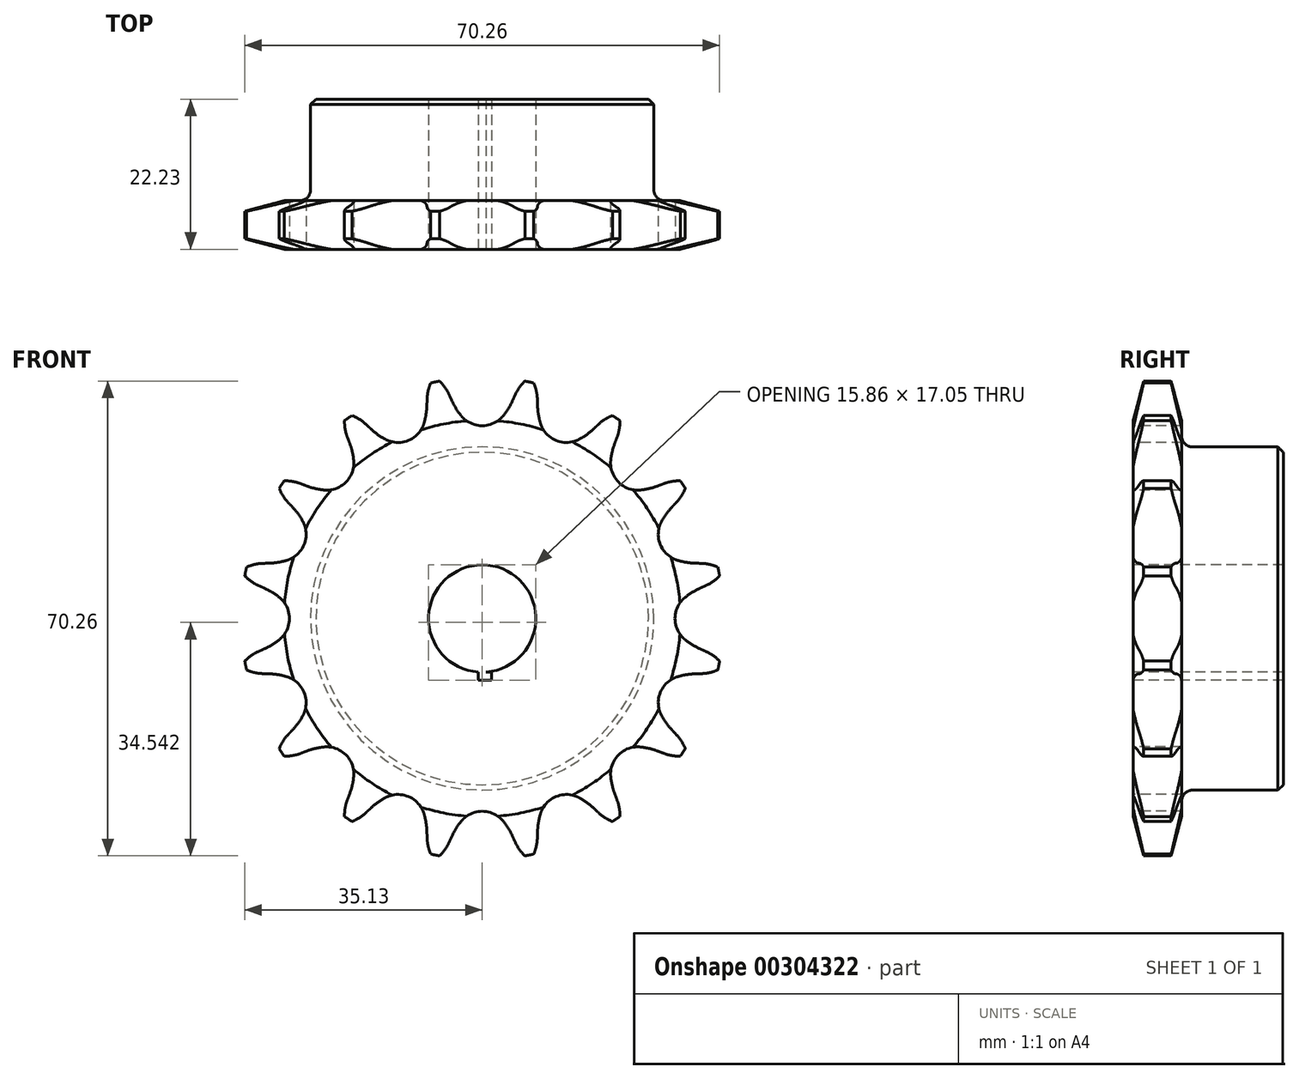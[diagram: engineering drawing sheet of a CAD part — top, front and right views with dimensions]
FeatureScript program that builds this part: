
annotation { "Feature Type Name" : "Feature", "Feature Type Description" : "" }
export const myFeature = defineFeature(function(context is Context, id is Id, definition is map)
    precondition{}
    {
        {
            var Q0;
            Q0=qCreatedBy(makeId("Right.planeOp"),FACE);
            var sketch = newSketch(context, id + "F0", { "sketchPlane" : qUnion([Q0])});
            skLineSegment(sketch, "E0", {"start": v(0, 0) * mm, "end": v(22.22, 0) * mm, "construction": true});
            skLineSegment(sketch, "E1", {"start": v(0, 35.69) * mm, "end": v(7.21, 35.69) * mm});
            skLineSegment(sketch, "E2", {"start": v(7.21, 35.69) * mm, "end": v(7.21, 25.4) * mm});
            skLineSegment(sketch, "E3", {"start": v(7.21, 25.4) * mm, "end": v(22.23, 25.4) * mm});
            skLineSegment(sketch, "E4", {"start": v(22.22, 25.4) * mm, "end": v(22.22, 7.94) * mm});
            skLineSegment(sketch, "E5", {"start": v(22.23, 7.94) * mm, "end": v(0, 7.94) * mm});
            skLineSegment(sketch, "E6", {"start": v(0, 7.94) * mm, "end": v(0, 35.69) * mm});
            skLineSegment(sketch, "E7.0.MirrorCS", {"start": v(0, -35.69) * mm, "end": v(7.21, -35.69) * mm});
            skLineSegment(sketch, "E7.1.MirrorCS", {"start": v(7.21, -35.69) * mm, "end": v(7.21, -25.4) * mm});
            skLineSegment(sketch, "E7.2.MirrorCS", {"start": v(22.23, -7.94) * mm, "end": v(0, -7.94) * mm});
            skLineSegment(sketch, "E7.3.MirrorCS", {"start": v(22.23, -25.4) * mm, "end": v(22.23, -7.94) * mm});
            skLineSegment(sketch, "E7.4.MirrorCS", {"start": v(7.21, -25.4) * mm, "end": v(22.23, -25.4) * mm});
            skLineSegment(sketch, "E7.5.MirrorCS", {"start": v(0, -7.94) * mm, "end": v(0, -35.69) * mm});
            skSolve(sketch);
        }
        {
            var Q0;
            Q0=makeQuery(id+"F0.imprint","IMPRINT",FACE,{"disambiguationData":[TD([[makeQuery(id+"F0.imprint","IMPRINT",EDGE,{"derivedFrom":sQuery(id+"F0.wireOp",EDGE,"E1")}),-1.0]])]});
            var Q1;
            Q1=sQuery(id+"F0.wireOp",EDGE,"E0");
            revolve(context, id + "F1", {"entities" : qUnion([Q0]), "axis" : qUnion([Q1]), "revolveType" : RevolveType.FULL});
        }
        {
            var Q0;
            Q0=makeQuery(id+"F1.opRevolve","SWEPT_EDGE",EDGE,{"disambiguationData":[OSD([sQuery(id+"F0.wireOp",EDGE,"E1"),sQuery(id+"F0.wireOp",EDGE,"E6")])]});
            var Q1;
            Q1=makeQuery(id+"F1.opRevolve","SWEPT_EDGE",EDGE,{"disambiguationData":[OSD([sQuery(id+"F0.wireOp",EDGE,"E1"),sQuery(id+"F0.wireOp",EDGE,"E2")])]});
            chamfer(context, id + "F2", {"entities" : qUnion([Q0, Q1]), "chamferType" : ChamferType.TWO_OFFSETS, "width1" : 6.35 * mm, "oppositeDirection" : false, "width2" : 1.57 * mm, "tangentPropagation" : true});
        }
        {
            var Q0;
            Q0=makeQuery(id+"F1.opRevolve","SWEPT_FACE",FACE,{"disambiguationData":[OSD([sQuery(id+"F0.wireOp",EDGE,"E6")])]});
            var sketch = newSketch(context, id + "F3", { "sketchPlane" : qUnion([Q0])});
            skCircle(sketch, "E8", {"center": v(0, 0) * mm, "radius": 32.55 * mm, "construction": true});
            skLineSegment(sketch, "E9", {"start": v(0, 0) * mm, "end": v(0, 32.55) * mm, "construction": true});
            skLineSegment(sketch, "E10", {"start": v(0, 32.55) * mm, "end": v(25.8, 32.55) * mm, "construction": true});
            skPoint(sketch, "E11", {"position": v(-10.88, 30.38) * mm});
            skPoint(sketch, "E12", {"position": v(4.95, 36.52) * mm});
            skLineSegment(sketch, "E13", {"start": v(0, 32.55) * mm, "end": v(4.95, 36.52) * mm, "construction": true});
            skLineSegment(sketch, "E14", {"start": v(4.95, 36.52) * mm, "end": v(-4.5, 32.26) * mm, "construction": true});
            skLineSegment(sketch, "E15", {"start": v(-4.5, 32.26) * mm, "end": v(-4.88, 33.1) * mm});
            skLineSegment(sketch, "E16", {"start": v(0, 0) * mm, "end": v(-7.12, 35.8) * mm, "construction": true});
            skArc(sketch, "E17", {"start": v(-7.12, 35.8) * mm, "mid": v(-15.95, 26.17) * mm, "end": v(-4.88, 33.1) * mm, "construction": true});
            skArc(sketch, "E18", {"start": v(-4.88, 33.1) * mm, "mid": v(-5.81, 34.6) * mm, "end": v(-7.12, 35.8) * mm});
            skArc(sketch, "E19", {"start": v(-3.14, 30.03) * mm, "mid": v(13.78, 41.93) * mm, "end": v(-4.5, 32.26) * mm, "construction": true});
            skArc(sketch, "E20", {"start": v(-4.5, 32.26) * mm, "mid": v(-3.89, 31.1) * mm, "end": v(-3.14, 30.03) * mm});
            skLineSegment(sketch, "E21", {"start": v(4.4, 12.5) * mm, "end": v(-4.88, 33.1) * mm, "construction": true});
            skArc(sketch, "E22.0.MirrorCS", {"start": v(4.5, 32.26) * mm, "mid": v(3.89, 31.1) * mm, "end": v(3.14, 30.03) * mm});
            skLineSegment(sketch, "E23.0.MirrorCS", {"start": v(4.5, 32.26) * mm, "end": v(4.88, 33.1) * mm});
            skArc(sketch, "E24.0.MirrorCS", {"start": v(4.88, 33.1) * mm, "mid": v(5.81, 34.6) * mm, "end": v(7.12, 35.8) * mm});
            skArc(sketch, "E25", {"start": v(-3.14, 30.03) * mm, "mid": v(0, 28.53) * mm, "end": v(3.14, 30.03) * mm});
            skArc(sketch, "E26", {"start": v(3.14, 30.03) * mm, "mid": v(0, 36.57) * mm, "end": v(-3.14, 30.03) * mm, "construction": true});
            skArc(sketch, "E27.1.0", {"start": v(-17.17, 28.7) * mm, "mid": v(-18.61, 29.74) * mm, "end": v(-20.28, 30.34) * mm});
            skLineSegment(sketch, "E27.1.1", {"start": v(-16.5, 28.08) * mm, "end": v(-17.17, 28.7) * mm});
            skArc(sketch, "E27.1.2", {"start": v(-16.5, 28.08) * mm, "mid": v(-15.5, 27.25) * mm, "end": v(-14.39, 26.55) * mm});
            skArc(sketch, "E27.1.3", {"start": v(-14.39, 26.55) * mm, "mid": v(-10.92, 26.36) * mm, "end": v(-8.6, 28.95) * mm});
            skArc(sketch, "E27.1.4", {"start": v(-8.19, 31.53) * mm, "mid": v(-8.3, 30.22) * mm, "end": v(-8.6, 28.95) * mm});
            skLineSegment(sketch, "E27.1.5", {"start": v(-8.19, 31.53) * mm, "end": v(-8.16, 32.44) * mm});
            skArc(sketch, "E27.1.6", {"start": v(-8.16, 32.44) * mm, "mid": v(-7.87, 34.19) * mm, "end": v(-7.12, 35.8) * mm});
            skArc(sketch, "E27.2.0", {"start": v(-26.85, 19.95) * mm, "mid": v(-28.57, 20.35) * mm, "end": v(-30.34, 20.28) * mm});
            skLineSegment(sketch, "E27.2.1", {"start": v(-26, 19.63) * mm, "end": v(-26.85, 19.95) * mm});
            skArc(sketch, "E27.2.2", {"start": v(-26, 19.63) * mm, "mid": v(-24.74, 19.24) * mm, "end": v(-23.45, 19.02) * mm});
            skArc(sketch, "E27.2.3", {"start": v(-23.45, 19.02) * mm, "mid": v(-20.17, 20.17) * mm, "end": v(-19.02, 23.45) * mm});
            skArc(sketch, "E27.2.4", {"start": v(-19.63, 26) * mm, "mid": v(-19.24, 24.74) * mm, "end": v(-19.02, 23.45) * mm});
            skLineSegment(sketch, "E27.2.5", {"start": v(-19.63, 26) * mm, "end": v(-19.95, 26.85) * mm});
            skArc(sketch, "E27.2.6", {"start": v(-19.95, 26.85) * mm, "mid": v(-20.35, 28.57) * mm, "end": v(-20.28, 30.34) * mm});
            skArc(sketch, "E27.3.0", {"start": v(-32.44, 8.16) * mm, "mid": v(-34.19, 7.87) * mm, "end": v(-35.8, 7.12) * mm});
            skLineSegment(sketch, "E27.3.1", {"start": v(-31.53, 8.19) * mm, "end": v(-32.44, 8.16) * mm});
            skArc(sketch, "E27.3.2", {"start": v(-31.53, 8.19) * mm, "mid": v(-30.22, 8.3) * mm, "end": v(-28.95, 8.6) * mm});
            skArc(sketch, "E27.3.3", {"start": v(-28.95, 8.6) * mm, "mid": v(-26.36, 10.92) * mm, "end": v(-26.55, 14.39) * mm});
            skArc(sketch, "E27.3.4", {"start": v(-28.08, 16.5) * mm, "mid": v(-27.25, 15.5) * mm, "end": v(-26.55, 14.39) * mm});
            skLineSegment(sketch, "E27.3.5", {"start": v(-28.08, 16.5) * mm, "end": v(-28.7, 17.17) * mm});
            skArc(sketch, "E27.3.6", {"start": v(-28.7, 17.17) * mm, "mid": v(-29.74, 18.61) * mm, "end": v(-30.34, 20.28) * mm});
            skArc(sketch, "E27.4.0", {"start": v(-33.1, -4.88) * mm, "mid": v(-34.6, -5.81) * mm, "end": v(-35.8, -7.12) * mm});
            skLineSegment(sketch, "E27.4.1", {"start": v(-32.26, -4.5) * mm, "end": v(-33.1, -4.88) * mm});
            skArc(sketch, "E27.4.2", {"start": v(-32.26, -4.5) * mm, "mid": v(-31.1, -3.89) * mm, "end": v(-30.03, -3.14) * mm});
            skArc(sketch, "E27.4.3", {"start": v(-30.03, -3.14) * mm, "mid": v(-28.53, 0) * mm, "end": v(-30.03, 3.14) * mm});
            skArc(sketch, "E27.4.4", {"start": v(-32.26, 4.5) * mm, "mid": v(-31.1, 3.89) * mm, "end": v(-30.03, 3.14) * mm});
            skLineSegment(sketch, "E27.4.5", {"start": v(-32.26, 4.5) * mm, "end": v(-33.1, 4.88) * mm});
            skArc(sketch, "E27.4.6", {"start": v(-33.1, 4.88) * mm, "mid": v(-34.6, 5.81) * mm, "end": v(-35.8, 7.12) * mm});
            skArc(sketch, "E27.5.0", {"start": v(-28.7, -17.17) * mm, "mid": v(-29.74, -18.61) * mm, "end": v(-30.34, -20.28) * mm});
            skLineSegment(sketch, "E27.5.1", {"start": v(-28.08, -16.5) * mm, "end": v(-28.7, -17.17) * mm});
            skArc(sketch, "E27.5.2", {"start": v(-28.08, -16.5) * mm, "mid": v(-27.25, -15.5) * mm, "end": v(-26.55, -14.39) * mm});
            skArc(sketch, "E27.5.3", {"start": v(-26.55, -14.39) * mm, "mid": v(-26.36, -10.92) * mm, "end": v(-28.95, -8.6) * mm});
            skArc(sketch, "E27.5.4", {"start": v(-31.53, -8.19) * mm, "mid": v(-30.22, -8.3) * mm, "end": v(-28.95, -8.6) * mm});
            skLineSegment(sketch, "E27.5.5", {"start": v(-31.53, -8.19) * mm, "end": v(-32.44, -8.16) * mm});
            skArc(sketch, "E27.5.6", {"start": v(-32.44, -8.16) * mm, "mid": v(-34.19, -7.87) * mm, "end": v(-35.8, -7.12) * mm});
            skArc(sketch, "E27.6.0", {"start": v(-19.95, -26.85) * mm, "mid": v(-20.35, -28.57) * mm, "end": v(-20.28, -30.34) * mm});
            skLineSegment(sketch, "E27.6.1", {"start": v(-19.63, -26) * mm, "end": v(-19.95, -26.85) * mm});
            skArc(sketch, "E27.6.2", {"start": v(-19.63, -26) * mm, "mid": v(-19.24, -24.74) * mm, "end": v(-19.02, -23.45) * mm});
            skArc(sketch, "E27.6.3", {"start": v(-19.02, -23.45) * mm, "mid": v(-20.17, -20.17) * mm, "end": v(-23.45, -19.02) * mm});
            skArc(sketch, "E27.6.4", {"start": v(-26, -19.63) * mm, "mid": v(-24.74, -19.24) * mm, "end": v(-23.45, -19.02) * mm});
            skLineSegment(sketch, "E27.6.5", {"start": v(-26, -19.63) * mm, "end": v(-26.85, -19.95) * mm});
            skArc(sketch, "E27.6.6", {"start": v(-26.85, -19.95) * mm, "mid": v(-28.57, -20.35) * mm, "end": v(-30.34, -20.28) * mm});
            skArc(sketch, "E27.7.0", {"start": v(-8.16, -32.44) * mm, "mid": v(-7.87, -34.19) * mm, "end": v(-7.12, -35.8) * mm});
            skLineSegment(sketch, "E27.7.1", {"start": v(-8.19, -31.53) * mm, "end": v(-8.16, -32.44) * mm});
            skArc(sketch, "E27.7.2", {"start": v(-8.19, -31.53) * mm, "mid": v(-8.3, -30.22) * mm, "end": v(-8.6, -28.95) * mm});
            skArc(sketch, "E27.7.3", {"start": v(-8.6, -28.95) * mm, "mid": v(-10.92, -26.36) * mm, "end": v(-14.39, -26.55) * mm});
            skArc(sketch, "E27.7.4", {"start": v(-16.5, -28.08) * mm, "mid": v(-15.5, -27.25) * mm, "end": v(-14.39, -26.55) * mm});
            skLineSegment(sketch, "E27.7.5", {"start": v(-16.5, -28.08) * mm, "end": v(-17.17, -28.7) * mm});
            skArc(sketch, "E27.7.6", {"start": v(-17.17, -28.7) * mm, "mid": v(-18.61, -29.74) * mm, "end": v(-20.28, -30.34) * mm});
            skArc(sketch, "E27.8.0", {"start": v(4.88, -33.1) * mm, "mid": v(5.81, -34.6) * mm, "end": v(7.12, -35.8) * mm});
            skLineSegment(sketch, "E27.8.1", {"start": v(4.5, -32.26) * mm, "end": v(4.88, -33.1) * mm});
            skArc(sketch, "E27.8.2", {"start": v(4.5, -32.26) * mm, "mid": v(3.89, -31.1) * mm, "end": v(3.14, -30.03) * mm});
            skArc(sketch, "E27.8.3", {"start": v(3.14, -30.03) * mm, "mid": v(0, -28.53) * mm, "end": v(-3.14, -30.03) * mm});
            skArc(sketch, "E27.8.4", {"start": v(-4.5, -32.26) * mm, "mid": v(-3.89, -31.1) * mm, "end": v(-3.14, -30.03) * mm});
            skLineSegment(sketch, "E27.8.5", {"start": v(-4.5, -32.26) * mm, "end": v(-4.88, -33.1) * mm});
            skArc(sketch, "E27.8.6", {"start": v(-4.88, -33.1) * mm, "mid": v(-5.81, -34.6) * mm, "end": v(-7.12, -35.8) * mm});
            skArc(sketch, "E27.9.0", {"start": v(17.17, -28.7) * mm, "mid": v(18.61, -29.74) * mm, "end": v(20.28, -30.34) * mm});
            skLineSegment(sketch, "E27.9.1", {"start": v(16.5, -28.08) * mm, "end": v(17.17, -28.7) * mm});
            skArc(sketch, "E27.9.2", {"start": v(16.5, -28.08) * mm, "mid": v(15.5, -27.25) * mm, "end": v(14.39, -26.55) * mm});
            skArc(sketch, "E27.9.3", {"start": v(14.39, -26.55) * mm, "mid": v(10.92, -26.36) * mm, "end": v(8.6, -28.95) * mm});
            skArc(sketch, "E27.9.4", {"start": v(8.19, -31.53) * mm, "mid": v(8.3, -30.22) * mm, "end": v(8.6, -28.95) * mm});
            skLineSegment(sketch, "E27.9.5", {"start": v(8.19, -31.53) * mm, "end": v(8.16, -32.44) * mm});
            skArc(sketch, "E27.9.6", {"start": v(8.16, -32.44) * mm, "mid": v(7.87, -34.19) * mm, "end": v(7.12, -35.8) * mm});
            skArc(sketch, "E27.10.0", {"start": v(26.85, -19.95) * mm, "mid": v(28.57, -20.35) * mm, "end": v(30.34, -20.28) * mm});
            skLineSegment(sketch, "E27.10.1", {"start": v(26, -19.63) * mm, "end": v(26.85, -19.95) * mm});
            skArc(sketch, "E27.10.2", {"start": v(26, -19.63) * mm, "mid": v(24.74, -19.24) * mm, "end": v(23.45, -19.02) * mm});
            skArc(sketch, "E27.10.3", {"start": v(23.45, -19.02) * mm, "mid": v(20.17, -20.17) * mm, "end": v(19.02, -23.45) * mm});
            skArc(sketch, "E27.10.4", {"start": v(19.63, -26) * mm, "mid": v(19.24, -24.74) * mm, "end": v(19.02, -23.45) * mm});
            skLineSegment(sketch, "E27.10.5", {"start": v(19.63, -26) * mm, "end": v(19.95, -26.85) * mm});
            skArc(sketch, "E27.10.6", {"start": v(19.95, -26.85) * mm, "mid": v(20.35, -28.57) * mm, "end": v(20.28, -30.34) * mm});
            skArc(sketch, "E27.11.0", {"start": v(32.44, -8.16) * mm, "mid": v(34.19, -7.87) * mm, "end": v(35.8, -7.12) * mm});
            skLineSegment(sketch, "E27.11.1", {"start": v(31.53, -8.19) * mm, "end": v(32.44, -8.16) * mm});
            skArc(sketch, "E27.11.2", {"start": v(31.53, -8.19) * mm, "mid": v(30.22, -8.3) * mm, "end": v(28.95, -8.6) * mm});
            skArc(sketch, "E27.11.3", {"start": v(28.95, -8.6) * mm, "mid": v(26.36, -10.92) * mm, "end": v(26.55, -14.39) * mm});
            skArc(sketch, "E27.11.4", {"start": v(28.08, -16.5) * mm, "mid": v(27.25, -15.5) * mm, "end": v(26.55, -14.39) * mm});
            skLineSegment(sketch, "E27.11.5", {"start": v(28.08, -16.5) * mm, "end": v(28.7, -17.17) * mm});
            skArc(sketch, "E27.11.6", {"start": v(28.7, -17.17) * mm, "mid": v(29.74, -18.61) * mm, "end": v(30.34, -20.28) * mm});
            skArc(sketch, "E27.12.0", {"start": v(33.1, 4.88) * mm, "mid": v(34.6, 5.81) * mm, "end": v(35.8, 7.12) * mm});
            skLineSegment(sketch, "E27.12.1", {"start": v(32.26, 4.5) * mm, "end": v(33.1, 4.88) * mm});
            skArc(sketch, "E27.12.2", {"start": v(32.26, 4.5) * mm, "mid": v(31.1, 3.89) * mm, "end": v(30.03, 3.14) * mm});
            skArc(sketch, "E27.12.3", {"start": v(30.03, 3.14) * mm, "mid": v(28.53, 0) * mm, "end": v(30.03, -3.14) * mm});
            skArc(sketch, "E27.12.4", {"start": v(32.26, -4.5) * mm, "mid": v(31.1, -3.89) * mm, "end": v(30.03, -3.14) * mm});
            skLineSegment(sketch, "E27.12.5", {"start": v(32.26, -4.5) * mm, "end": v(33.1, -4.88) * mm});
            skArc(sketch, "E27.12.6", {"start": v(33.1, -4.88) * mm, "mid": v(34.6, -5.81) * mm, "end": v(35.8, -7.12) * mm});
            skArc(sketch, "E27.13.0", {"start": v(28.7, 17.17) * mm, "mid": v(29.74, 18.61) * mm, "end": v(30.34, 20.28) * mm});
            skLineSegment(sketch, "E27.13.1", {"start": v(28.08, 16.5) * mm, "end": v(28.7, 17.17) * mm});
            skArc(sketch, "E27.13.2", {"start": v(28.08, 16.5) * mm, "mid": v(27.25, 15.5) * mm, "end": v(26.55, 14.39) * mm});
            skArc(sketch, "E27.13.3", {"start": v(26.55, 14.39) * mm, "mid": v(26.36, 10.92) * mm, "end": v(28.95, 8.6) * mm});
            skArc(sketch, "E27.13.4", {"start": v(31.53, 8.19) * mm, "mid": v(30.22, 8.3) * mm, "end": v(28.95, 8.6) * mm});
            skLineSegment(sketch, "E27.13.5", {"start": v(31.53, 8.19) * mm, "end": v(32.44, 8.16) * mm});
            skArc(sketch, "E27.13.6", {"start": v(32.44, 8.16) * mm, "mid": v(34.19, 7.87) * mm, "end": v(35.8, 7.12) * mm});
            skArc(sketch, "E27.14.0", {"start": v(19.95, 26.85) * mm, "mid": v(20.35, 28.57) * mm, "end": v(20.28, 30.34) * mm});
            skLineSegment(sketch, "E27.14.1", {"start": v(19.63, 26) * mm, "end": v(19.95, 26.85) * mm});
            skArc(sketch, "E27.14.2", {"start": v(19.63, 26) * mm, "mid": v(19.24, 24.74) * mm, "end": v(19.02, 23.45) * mm});
            skArc(sketch, "E27.14.3", {"start": v(19.02, 23.45) * mm, "mid": v(20.17, 20.17) * mm, "end": v(23.45, 19.02) * mm});
            skArc(sketch, "E27.14.4", {"start": v(26, 19.63) * mm, "mid": v(24.74, 19.24) * mm, "end": v(23.45, 19.02) * mm});
            skLineSegment(sketch, "E27.14.5", {"start": v(26, 19.63) * mm, "end": v(26.85, 19.95) * mm});
            skArc(sketch, "E27.14.6", {"start": v(26.85, 19.95) * mm, "mid": v(28.57, 20.35) * mm, "end": v(30.34, 20.28) * mm});
            skArc(sketch, "E27.15.0", {"start": v(8.16, 32.44) * mm, "mid": v(7.87, 34.19) * mm, "end": v(7.12, 35.8) * mm});
            skLineSegment(sketch, "E27.15.1", {"start": v(8.19, 31.53) * mm, "end": v(8.16, 32.44) * mm});
            skArc(sketch, "E27.15.2", {"start": v(8.19, 31.53) * mm, "mid": v(8.3, 30.22) * mm, "end": v(8.6, 28.95) * mm});
            skArc(sketch, "E27.15.3", {"start": v(8.6, 28.95) * mm, "mid": v(10.92, 26.36) * mm, "end": v(14.39, 26.55) * mm});
            skArc(sketch, "E27.15.4", {"start": v(16.5, 28.08) * mm, "mid": v(15.5, 27.25) * mm, "end": v(14.39, 26.55) * mm});
            skLineSegment(sketch, "E27.15.5", {"start": v(16.5, 28.08) * mm, "end": v(17.17, 28.7) * mm});
            skArc(sketch, "E27.15.6", {"start": v(17.17, 28.7) * mm, "mid": v(18.61, 29.74) * mm, "end": v(20.28, 30.34) * mm});
            skSolve(sketch);
        }
        {
            var Q0;
            Q0=qSketchRegion(id+"F3",true);
            extrude(context, id + "F4", {"entities" : qUnion([Q0]), "operationType" : NewBodyOperationType.INTERSECT, "endBound" : BoundingType.THROUGH_ALL, "oppositeDirection" : true, "depth" : 25.4 * mm});
        }
        {
            var Q0;
            Q0=makeQuery(id+"F1.opRevolve","SWEPT_EDGE",EDGE,{"disambiguationData":[OSD([sQuery(id+"F0.wireOp",EDGE,"E2"),sQuery(id+"F0.wireOp",EDGE,"E3")])]});
            fillet(context, id + "F5", {"entities" : qUnion([Q0]), "radius" : 1.59 * mm, "tangentPropagation" : true, "allowEdgeOverflow" : false});
        }
        {
            var Q0;
            Q0=makeQuery(id+"F1.opRevolve","SWEPT_EDGE",EDGE,{"disambiguationData":[OSD([sQuery(id+"F0.wireOp",EDGE,"E3"),sQuery(id+"F0.wireOp",EDGE,"E4")])]});
            chamfer(context, id + "F6", {"entities" : qUnion([Q0]), "width" : 0.8 * mm, "tangentPropagation" : true});
        }
        {
            var Q0;
            {var subQ1=sQuery(id+"F0.wireOp",EDGE,"E6");Q0=makeQuery(id+"F3.imprint","IMPRINT",FACE,{"disambiguationData":[TD([[makeQuery(id+"F3.imprint","IMPRINT",EDGE,{"derivedFrom":makeQuery(id+"F1.opRevolve","SWEPT_EDGE",EDGE,{"disambiguationData":[OSD([sQuery(id+"F0.wireOp",EDGE,"E5"),subQ1])]})}),-1.0]])]});}
            var sketch = newSketch(context, id + "F7", { "sketchPlane" : qUnion([Q0])});
            skLineSegment(sketch, "E28.bottom", {"start": v(-0.57, -7.92) * mm, "end": v(1.4, -7.92) * mm});
            skLineSegment(sketch, "E28.top", {"start": v(-0.57, -9.11) * mm, "end": v(1.4, -9.11) * mm});
            skLineSegment(sketch, "E28.left", {"start": v(-0.57, -7.92) * mm, "end": v(-0.57, -9.11) * mm});
            skLineSegment(sketch, "E28.right", {"start": v(1.4, -7.92) * mm, "end": v(1.4, -9.11) * mm});
            skSolve(sketch);
        }
        {
            var Q0;
            Q0 = qSketchRegion(id + "F7", true);
            extrude(context, id + "F8", {"entities" : qUnion([Q0]), "operationType" : NewBodyOperationType.REMOVE, "oppositeDirection" : true, "depth" : 25.4 * mm});
        }
    });
